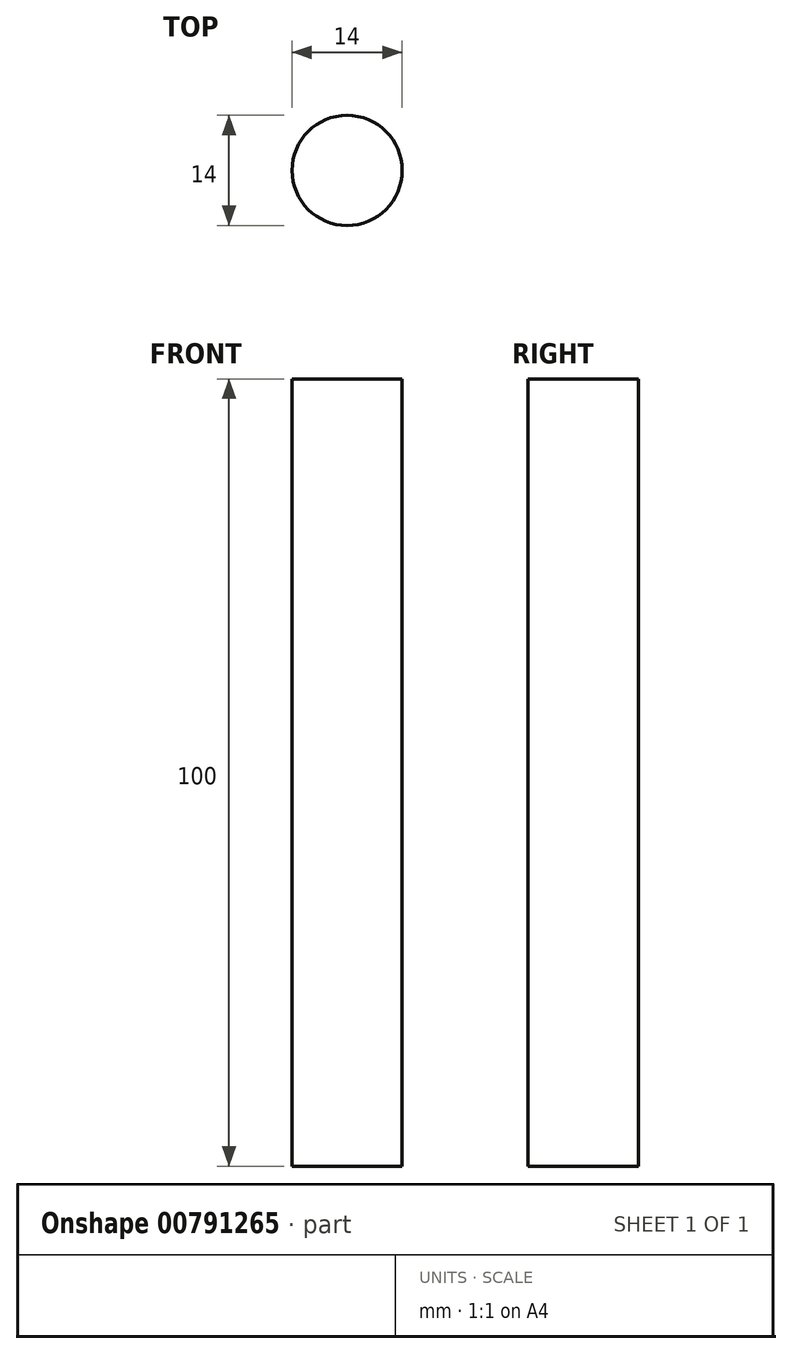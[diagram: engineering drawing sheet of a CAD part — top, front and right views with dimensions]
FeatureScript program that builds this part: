
annotation { "Feature Type Name" : "Feature", "Feature Type Description" : "" }
export const myFeature = defineFeature(function(context is Context, id is Id, definition is map)
    precondition{}
    {
        {
            var Q0;
            Q0=qCreatedBy(makeId("Top.planeOp"),FACE);
            var sketch = newSketch(context, id + "F0", { "sketchPlane" : qUnion([Q0])});
            skCircle(sketch, "E0", {"center": v(0, 0) * mm, "radius": 7 * mm});
            skSolve(sketch);
        }
        {
            var Q0;
            Q0=makeQuery(id+"F0.imprint","IMPRINT",FACE,{"disambiguationData":[TD([[makeQuery(id+"F0.imprint","IMPRINT",EDGE,{"derivedFrom":sQuery(id+"F0.wireOp",EDGE,"E0")}),1.0]])]});
            extrude(context, id + "F1", {"entities" : qUnion([Q0]), "depth" : 100 * mm, "offsetDistance" : 25 * mm});
        }
    });
